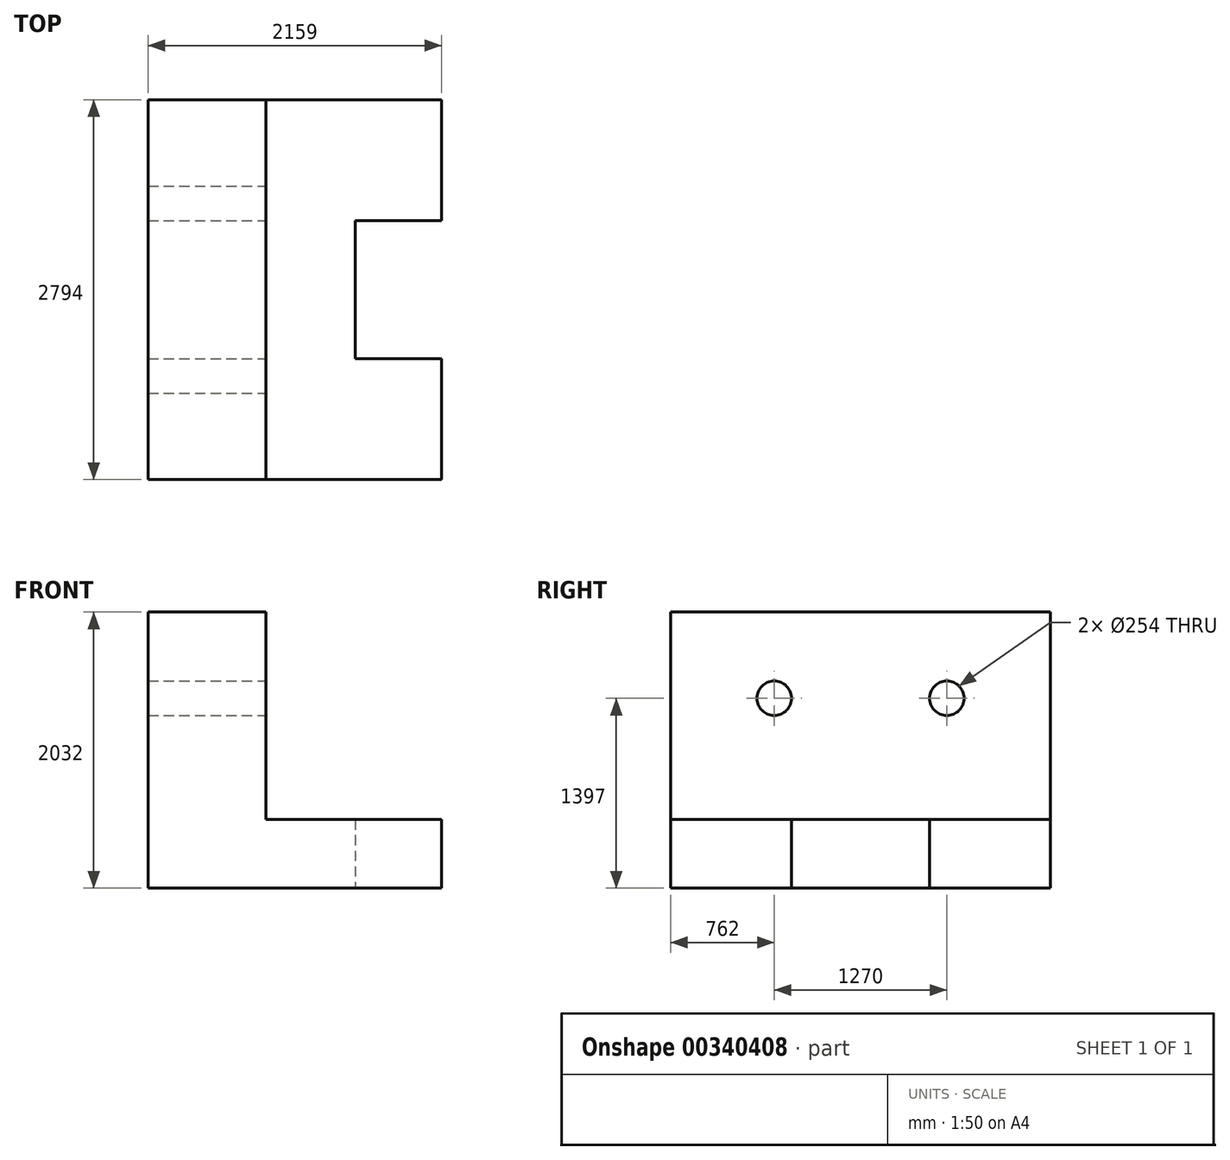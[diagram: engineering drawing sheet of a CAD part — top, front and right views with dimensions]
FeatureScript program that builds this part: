
annotation { "Feature Type Name" : "Feature", "Feature Type Description" : "" }
export const myFeature = defineFeature(function(context is Context, id is Id, definition is map)
    precondition{}
    {
        {
            var Q0;
            Q0=qCreatedBy(makeId("Top.planeOp"),FACE);
            var sketch = newSketch(context, id + "F0", { "sketchPlane" : qUnion([Q0])});
            skLineSegment(sketch, "E0", {"start": v(0, 0) * mm, "end": v(0, 2794) * mm});
            skLineSegment(sketch, "E1", {"start": v(0, 2794) * mm, "end": v(635, 2794) * mm});
            skLineSegment(sketch, "E2", {"start": v(635, 2794) * mm, "end": v(635, 0) * mm});
            skLineSegment(sketch, "E3", {"start": v(635, 0) * mm, "end": v(0, 0) * mm});
            skLineSegment(sketch, "E4", {"start": v(635, 0) * mm, "end": v(2159, 0) * mm});
            skLineSegment(sketch, "E5", {"start": v(2159, 0) * mm, "end": v(2159, 889) * mm});
            skLineSegment(sketch, "E6", {"start": v(2159, 889) * mm, "end": v(1524, 889) * mm});
            skLineSegment(sketch, "E7", {"start": v(1524, 889) * mm, "end": v(1524, 1905) * mm});
            skLineSegment(sketch, "E8", {"start": v(1524, 1905) * mm, "end": v(2159, 1905) * mm});
            skLineSegment(sketch, "E9", {"start": v(2159, 1905) * mm, "end": v(2159, 2794) * mm});
            skLineSegment(sketch, "E10", {"start": v(2159, 2794) * mm, "end": v(635, 2794) * mm});
            skSolve(sketch);
        }
        {
            var Q0;
            Q0 = qSketchRegion(id + "F0", true);
            extrude(context, id + "F1", {"entities" : qUnion([Q0]), "depth" : 2032 * mm});
        }
        {
            var Q0;
            Q0=makeQuery(id+"F1.opExtrude","SWEPT_FACE",FACE,{"disambiguationData":[OSD([sQuery(id+"F0.wireOp",EDGE,"E3"),sQuery(id+"F0.wireOp",EDGE,"E4")])]});
            var sketch = newSketch(context, id + "F2", { "sketchPlane" : qUnion([Q0])});
            skLineSegment(sketch, "E11", {"start": v(1514.68, 2032) * mm, "end": v(1514.68, 504.62) * mm});
            skLineSegment(sketch, "E12", {"start": v(1514.68, 504.62) * mm, "end": v(2159, 504.62) * mm});
            skLineSegment(sketch, "E13", {"start": v(2159, 504.62) * mm, "end": v(2159, 0) * mm});
            skLineSegment(sketch, "E14", {"start": v(2159, 0) * mm, "end": v(0, 0) * mm});
            skLineSegment(sketch, "E15", {"start": v(0, 0) * mm, "end": v(0, 2032) * mm});
            skLineSegment(sketch, "E16", {"start": v(0, 2032) * mm, "end": v(1514.68, 2032) * mm});
            skSolve(sketch);
        }
        {
            var Q0;
            {var subQ0=sQuery(id+"F2.wireOp",EDGE,"E11");Q0=makeQuery(id+"F2.imprint","IMPRINT",FACE,{"disambiguationData":[TD([[makeQuery(id+"F2.imprint","IMPRINT",EDGE,{"derivedFrom":subQ0}),1.0]])]});}
            extrude(context, id + "F3", {"entities" : qUnion([Q0]), "operationType" : NewBodyOperationType.REMOVE, "endBound" : BoundingType.THROUGH_ALL, "oppositeDirection" : true, "depth" : 25.4 * mm});
        }
        {
            var Q0;
            Q0=makeQuery(id+"F3.boolean.opBoolean","COPY",FACE,{"derivedFrom":makeQuery(id+"F3.opExtrude","SWEPT_FACE",FACE,{"disambiguationData":[OSD([sQuery(id+"F2.wireOp",EDGE,"E11")])]})});
            var sketch = newSketch(context, id + "F4", { "sketchPlane" : qUnion([Q0])});
            skCircle(sketch, "E17", {"center": v(762, 1397) * mm, "radius": 127 * mm});
            skCircle(sketch, "E18", {"center": v(2032, 1397) * mm, "radius": 127 * mm});
            skSolve(sketch);
        }
        {
            var Q0;
            Q0=makeQuery(id+"F4.imprint","IMPRINT",FACE,{"disambiguationData":[TD([[makeQuery(id+"F4.imprint","IMPRINT",EDGE,{"derivedFrom":sQuery(id+"F4.wireOp",EDGE,"E18")}),1.0]])]});
            var Q1;
            Q1=makeQuery(id+"F4.imprint","IMPRINT",FACE,{"disambiguationData":[TD([[makeQuery(id+"F4.imprint","IMPRINT",EDGE,{"derivedFrom":sQuery(id+"F4.wireOp",EDGE,"E17")}),1.0]])]});
            extrude(context, id + "F5", {"entities" : qUnion([Q0, Q1]), "operationType" : NewBodyOperationType.REMOVE, "endBound" : BoundingType.THROUGH_ALL, "oppositeDirection" : true, "depth" : 25.4 * mm});
        }
        {
            var Q0;
            Q0=makeQuery(id+"F1.opExtrude","SWEPT_FACE",FACE,{"disambiguationData":[OSD([sQuery(id+"F0.wireOp",EDGE,"E3"),sQuery(id+"F0.wireOp",EDGE,"E4")])]});
            var sketch = newSketch(context, id + "F6", { "sketchPlane" : qUnion([Q0])});
            skLineSegment(sketch, "E19", {"start": v(866.25, 2032) * mm, "end": v(866.25, 504.62) * mm});
            skLineSegment(sketch, "E20", {"start": v(866.25, 504.62) * mm, "end": v(1514.68, 504.62) * mm});
            skLineSegment(sketch, "E21", {"start": v(1514.68, 504.62) * mm, "end": v(1514.68, 2032) * mm});
            skLineSegment(sketch, "E22", {"start": v(1514.68, 2032) * mm, "end": v(866.25, 2032) * mm});
            skSolve(sketch);
        }
        {
            var Q0;
            Q0=makeQuery(id+"F6.imprint","IMPRINT",FACE,{"disambiguationData":[TD([[makeQuery(id+"F6.imprint","IMPRINT",EDGE,{"derivedFrom":sQuery(id+"F6.wireOp",EDGE,"E19")}),1.0]])]});
            extrude(context, id + "F7", {"entities" : qUnion([Q0]), "operationType" : NewBodyOperationType.REMOVE, "endBound" : BoundingType.THROUGH_ALL, "oppositeDirection" : true, "depth" : 25.4 * mm});
        }
    });
